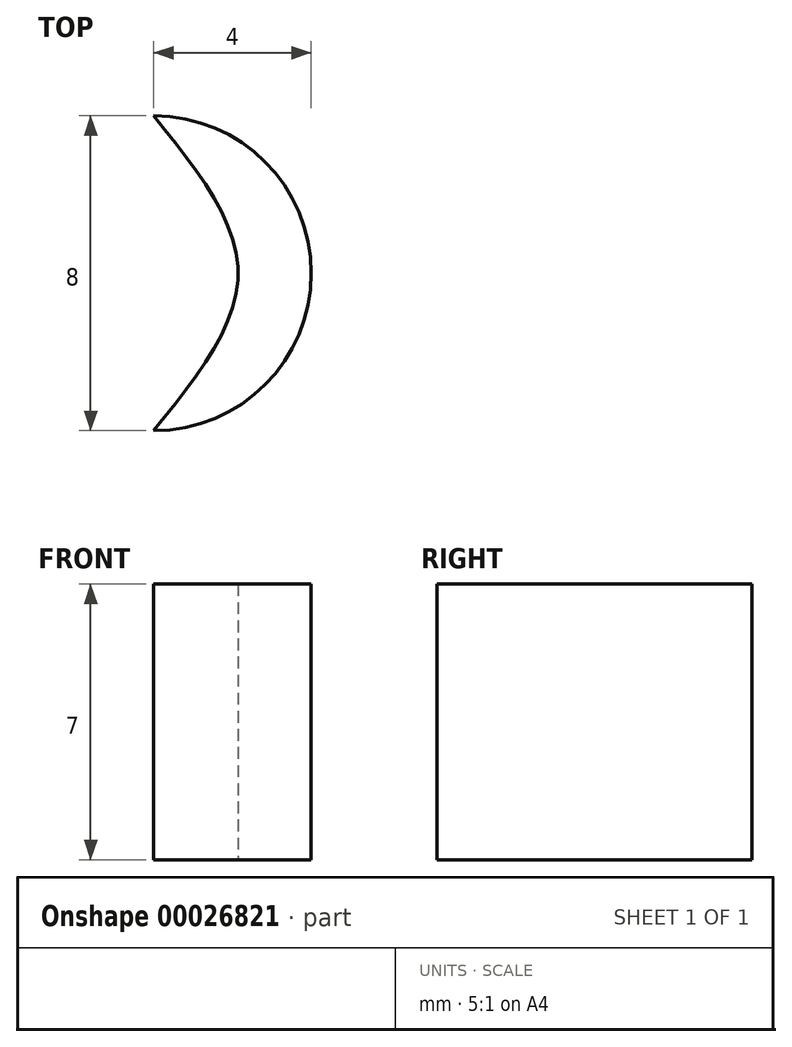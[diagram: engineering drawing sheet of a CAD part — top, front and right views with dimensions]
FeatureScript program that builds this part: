
annotation { "Feature Type Name" : "Feature", "Feature Type Description" : "" }
export const myFeature = defineFeature(function(context is Context, id is Id, definition is map)
    precondition{}
    {
        {
            var Q0;
            Q0=qCreatedBy(makeId("Top.planeOp"),FACE);
            var sketch = newSketch(context, id + "F0", { "sketchPlane" : qUnion([Q0])});
            skArc(sketch, "E0", {"start": v(0, -4) * mm, "mid": v(4, 0) * mm, "end": v(0, 4) * mm});
            skFitSpline(sketch, "E1", {"points": [v(0, 4) * mm, v(2.14, 0) * mm, v(0, -4) * mm], "startDerivative": vector(6.43, -8) * mm, "endDerivative": vector(-6.43, -8) * mm});
            skSolve(sketch);
        }
        {
            var Q0;
            Q0 = qSketchRegion(id + "F0", true);
            extrude(context, id + "F1", {"entities" : qUnion([Q0]), "depth" : 7 * mm});
        }
    });
